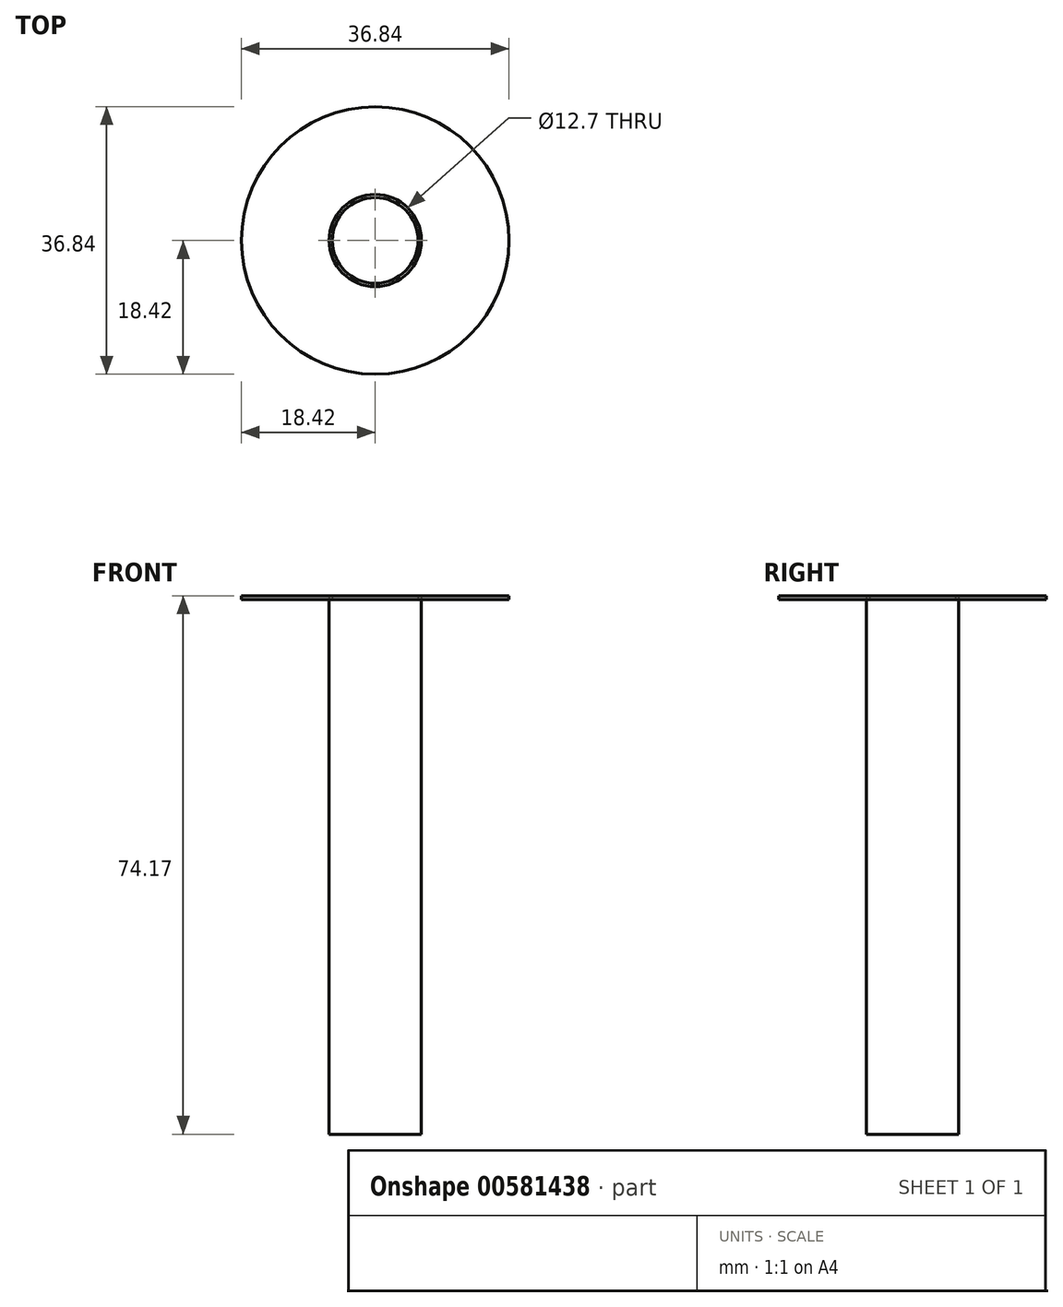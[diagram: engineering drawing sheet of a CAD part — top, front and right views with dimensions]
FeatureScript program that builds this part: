
annotation { "Feature Type Name" : "Feature", "Feature Type Description" : "" }
export const myFeature = defineFeature(function(context is Context, id is Id, definition is map)
    precondition{}
    {
        {
            var Q0;
            Q0=qCreatedBy(makeId("Top.planeOp"),FACE);
            var sketch = newSketch(context, id + "F0", { "sketchPlane" : qUnion([Q0])});
            skCircle(sketch, "E0", {"center": v(0, 0) * mm, "radius": 6.35 * mm});
            skSolve(sketch);
        }
        {
            var Q0;
            Q0=makeQuery(id+"F0.imprint","IMPRINT",FACE,{"disambiguationData":[TD([[makeQuery(id+"F0.imprint","IMPRINT",EDGE,{"derivedFrom":sQuery(id+"F0.wireOp",EDGE,"E0")}),1.0]])]});
            extrude(context, id + "F1", {"entities" : qUnion([Q0]), "depth" : 73.66 * mm, "offsetDistance" : 25.4 * mm});
        }
        {
            var Q0;
            Q0=makeQuery(id+"F1.opExtrude","CAP_FACE",FACE,{"disambiguationData":[OSD([sQuery(id+"F0.wireOp",EDGE,"E0")])],"isStart":false});
            var sketch = newSketch(context, id + "F2", { "sketchPlane" : qUnion([Q0])});
            skCircle(sketch, "E1", {"center": v(0, 0) * mm, "radius": 18.41 * mm});
            skCircle(sketch, "E2", {"center": v(0, 0) * mm, "radius": 5.9 * mm});
            skSolve(sketch);
        }
        {
            var Q0;
            Q0=makeQuery(id+"F2.imprint","IMPRINT",FACE,{"disambiguationData":[TD([[makeQuery(id+"F2.imprint","IMPRINT",EDGE,{"derivedFrom":sQuery(id+"F2.wireOp",EDGE,"E1")}),1.0]])]});
            var Q1;
            Q1=makeQuery(id+"F2.imprint","IMPRINT",FACE,{"disambiguationData":[TD([[makeQuery(id+"F2.imprint","IMPRINT",EDGE,{"derivedFrom":sQuery(id+"F2.wireOp",EDGE,"E2")}),1.0]])]});
            extrude(context, id + "F3", {"entities" : qUnion([Q0, Q1]), "depth" : 0.5 * mm, "offsetDistance" : 25.4 * mm});
        }
    });
